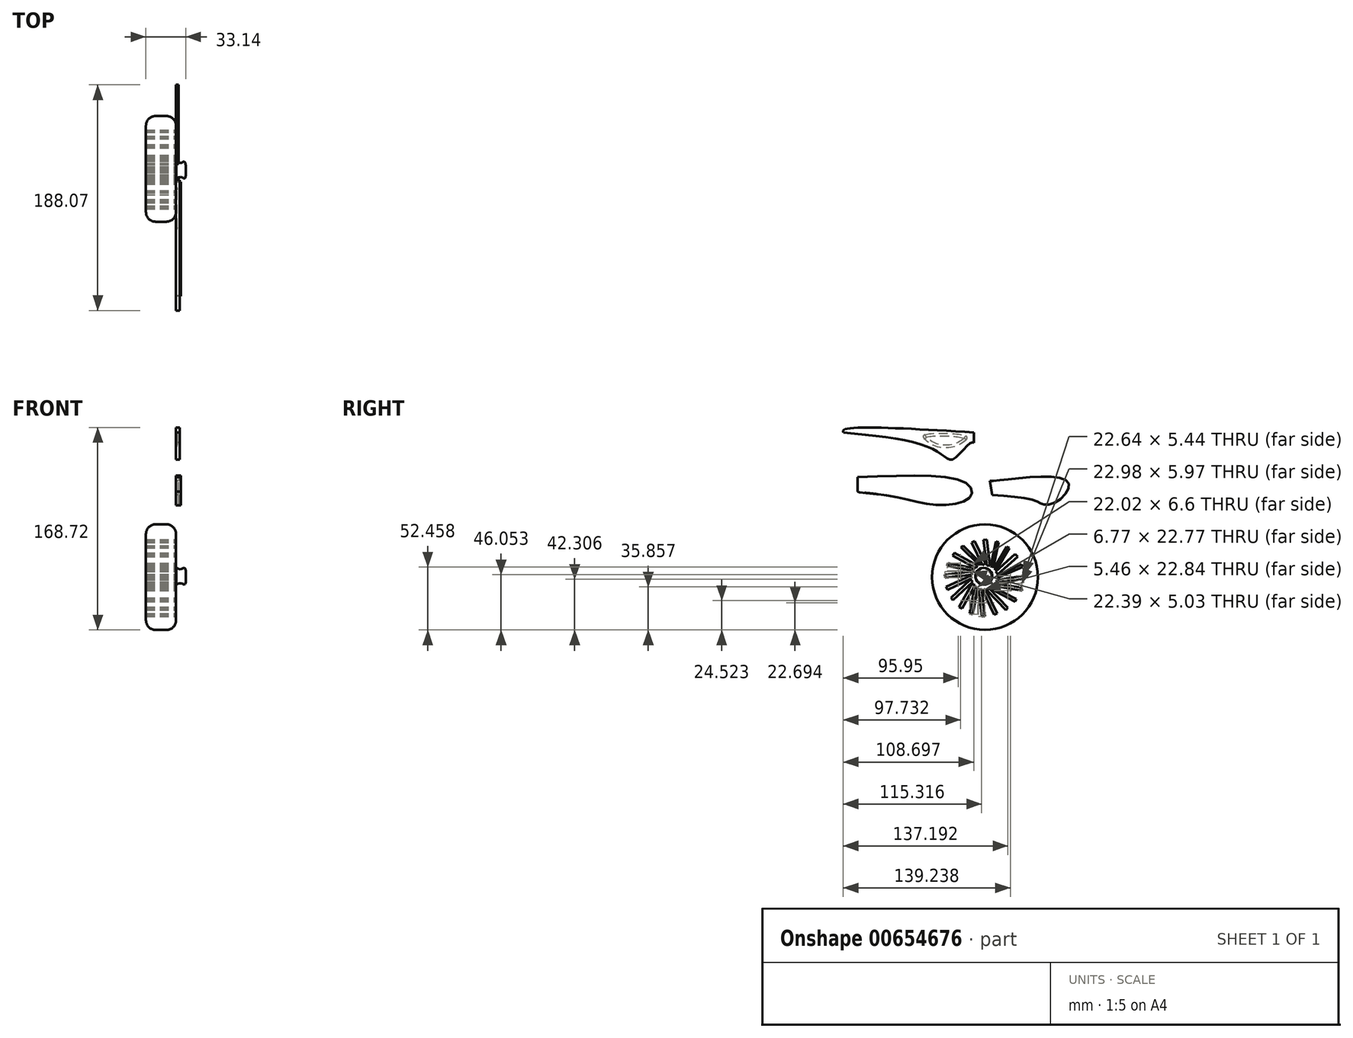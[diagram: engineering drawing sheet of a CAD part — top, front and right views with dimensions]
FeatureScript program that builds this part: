
annotation { "Feature Type Name" : "Feature", "Feature Type Description" : "" }
export const myFeature = defineFeature(function(context is Context, id is Id, definition is map)
    precondition{}
    {
        {
            var Q0;
            Q0=qCreatedBy(makeId("Right.planeOp"),FACE);
            var sketch = newSketch(context, id + "F0", { "sketchPlane" : qUnion([Q0])});
            skFitSpline(sketch, "E0", {"points": [v(-61.2, 25.53) * mm, v(9.14, 13.55) * mm, v(24.54, 4.13) * mm, v(30.7, 3.62) * mm, v(44.56, 16.97) * mm, v(47.3, 16.8) * mm], "startDerivative": vector(208.43, -21.43) * mm, "endDerivative": vector(29.28, -15.69) * mm});
            skFitSpline(sketch, "E1", {"points": [v(-61.2, 25.53) * mm, v(-61.2, 27.58) * mm, v(47.3, 25.53) * mm], "startDerivative": vector(-7.46, 18.15) * mm, "endDerivative": vector(177.67, -10.83) * mm});
            skLineSegment(sketch, "E2", {"start": v(47.3, 16.8) * mm, "end": v(47.3, 25.53) * mm});
            skSolve(sketch);
        }
        {
            var Q0;
            Q0=makeQuery(id+"F0.imprint","IMPRINT",FACE,{"disambiguationData":[TD([[makeQuery(id+"F0.imprint","IMPRINT",EDGE,{"derivedFrom":sQuery(id+"F0.wireOp",EDGE,"E0")}),1.0]])]});
            extrude(context, id + "F1", {"entities" : qUnion([Q0]), "depth" : 3 * mm, "offsetDistance" : 25.4 * mm});
        }
        {
            var Q0;
            Q0=qCreatedBy(makeId("Right.planeOp"),FACE);
            var sketch = newSketch(context, id + "F2", { "sketchPlane" : qUnion([Q0])});
            skFitSpline(sketch, "E3", {"points": [v(5.41, 21.07) * mm, v(5.19, 21.5) * mm, v(5.02, 22.27) * mm, v(5.24, 22.9) * mm, v(6.38, 23.6) * mm, v(8.34, 24.16) * mm, v(11.68, 24.6) * mm, v(16.33, 24.87) * mm, v(18.57, 24.92) * mm, v(23.05, 24.91) * mm, v(27.45, 24.72) * mm, v(32.7, 24.28) * mm, v(36.42, 23.76) * mm, v(38.73, 23.22) * mm, v(40.53, 22.6) * mm, v(41.13, 22.23) * mm, v(41.55, 21.71) * mm, v(41.66, 21.04) * mm, v(41.41, 20.27) * mm, v(40.6, 19.08) * mm, v(38.85, 17.67) * mm, v(36.95, 16.38) * mm, v(34.7, 15.13) * mm, v(32.34, 14.11) * mm, v(29.64, 13.3) * mm, v(26.9, 12.82) * mm, v(23.76, 12.62) * mm, v(20.63, 12.82) * mm, v(17.77, 13.37) * mm, v(14.7, 14.36) * mm, v(12.81, 15.2) * mm, v(10.72, 16.4) * mm, v(9.05, 17.5) * mm, v(7.02, 19.16) * mm, v(6.25, 19.87) * mm, v(5.41, 21.07) * mm]});
            skSolve(sketch);
        }
        {
            var Q0;
            Q0=qCreatedBy(makeId("Right.planeOp"),FACE);
            var sketch = newSketch(context, id + "F3", { "sketchPlane" : qUnion([Q0])});
            skCircle(sketch, "E4", {"center": v(56.51, -95.04) * mm, "radius": 44.03 * mm});
            skSolve(sketch);
        }
        {
            var Q0;
            Q0 = qSketchRegion(id + "F3", true);
            extrude(context, id + "F4", {"entities" : qUnion([Q0]), "oppositeDirection" : true, "depth" : 25 * mm, "offsetDistance" : 25 * mm});
        }
        {
            var Q0;
            Q0=makeQuery(id+"F4.opExtrude","SWEPT_FACE",FACE,{"disambiguationData":[OSD([sQuery(id+"F3.wireOp",EDGE,"E4")])]});
            fillet(context, id + "F5", {"entities" : qUnion([Q0]), "radius" : 8 * mm, "tangentPropagation" : true, "allowEdgeOverflow" : false});
        }
        {
            var Q0;
            Q0=qCreatedBy(makeId("Right.planeOp"),FACE);
            var sketch = newSketch(context, id + "F6", { "sketchPlane" : qUnion([Q0])});
            skLineSegment(sketch, "E5", {"start": v(36.45, -70.1) * mm, "end": v(38.25, -68.9) * mm});
            skLineSegment(sketch, "E6", {"start": v(38.25, -68.9) * mm, "end": v(53.15, -83.57) * mm});
            skLineSegment(sketch, "E7", {"start": v(53.15, -83.57) * mm, "end": v(51.66, -85.08) * mm});
            skLineSegment(sketch, "E8", {"start": v(51.66, -85.08) * mm, "end": v(36.45, -70.1) * mm});
            skLineSegment(sketch, "E9", {"start": v(30.92, -74.91) * mm, "end": v(50.15, -85.25) * mm});
            skLineSegment(sketch, "E10", {"start": v(50.15, -85.25) * mm, "end": v(48.95, -87.49) * mm});
            skLineSegment(sketch, "E11", {"start": v(48.95, -87.49) * mm, "end": v(29.5, -77.03) * mm});
            skLineSegment(sketch, "E12", {"start": v(29.5, -77.03) * mm, "end": v(30.92, -74.91) * mm});
            skLineSegment(sketch, "E13", {"start": v(25.67, -83.3) * mm, "end": v(47.2, -87.49) * mm});
            skLineSegment(sketch, "E14", {"start": v(47.2, -87.49) * mm, "end": v(46.72, -89.9) * mm});
            skLineSegment(sketch, "E15", {"start": v(46.72, -89.9) * mm, "end": v(25.17, -85.71) * mm});
            skLineSegment(sketch, "E16", {"start": v(25.17, -85.71) * mm, "end": v(25.67, -83.3) * mm});
            skLineSegment(sketch, "E17", {"start": v(23.2, -92.92) * mm, "end": v(45.34, -90.5) * mm});
            skLineSegment(sketch, "E18", {"start": v(45.34, -90.5) * mm, "end": v(45.6, -92.8) * mm});
            skLineSegment(sketch, "E19", {"start": v(45.6, -92.8) * mm, "end": v(23.56, -95.52) * mm});
            skLineSegment(sketch, "E20", {"start": v(23.56, -95.52) * mm, "end": v(23.2, -92.92) * mm});
            skLineSegment(sketch, "E21", {"start": v(24.02, -103.15) * mm, "end": v(44.38, -93.78) * mm});
            skLineSegment(sketch, "E22", {"start": v(44.38, -93.78) * mm, "end": v(45.45, -96.1) * mm});
            skLineSegment(sketch, "E23", {"start": v(45.45, -96.1) * mm, "end": v(25.25, -105.63) * mm});
            skLineSegment(sketch, "E24", {"start": v(25.25, -105.63) * mm, "end": v(24.02, -103.15) * mm});
            skLineSegment(sketch, "E25", {"start": v(29.97, -114.23) * mm, "end": v(46.3, -99.12) * mm});
            skLineSegment(sketch, "E26", {"start": v(46.3, -99.12) * mm, "end": v(44.55, -97.23) * mm});
            skLineSegment(sketch, "E27", {"start": v(44.55, -97.23) * mm, "end": v(28.13, -112.42) * mm});
            skLineSegment(sketch, "E28", {"start": v(28.13, -112.42) * mm, "end": v(29.97, -114.23) * mm});
            skLineSegment(sketch, "E29", {"start": v(37.28, -121.33) * mm, "end": v(48.11, -102) * mm});
            skLineSegment(sketch, "E30", {"start": v(48.11, -102) * mm, "end": v(45.77, -100.73) * mm});
            skLineSegment(sketch, "E31", {"start": v(45.77, -100.73) * mm, "end": v(34.94, -120.05) * mm});
            skLineSegment(sketch, "E32", {"start": v(34.94, -120.05) * mm, "end": v(37.28, -121.31) * mm});
            skLineSegment(sketch, "E33", {"start": v(43.76, -125.47) * mm, "end": v(48, -103.15) * mm});
            skLineSegment(sketch, "E34", {"start": v(48, -103.15) * mm, "end": v(50.53, -103.63) * mm});
            skLineSegment(sketch, "E35", {"start": v(50.53, -103.63) * mm, "end": v(46.3, -125.92) * mm});
            skLineSegment(sketch, "E36", {"start": v(46.3, -125.92) * mm, "end": v(43.76, -125.47) * mm});
            skLineSegment(sketch, "E37", {"start": v(56.5, -127.45) * mm, "end": v(53.72, -104.95) * mm});
            skLineSegment(sketch, "E38", {"start": v(53.72, -104.95) * mm, "end": v(51.04, -105.28) * mm});
            skLineSegment(sketch, "E39", {"start": v(51.04, -105.28) * mm, "end": v(53.82, -127.79) * mm});
            skLineSegment(sketch, "E40", {"start": v(53.82, -127.79) * mm, "end": v(56.5, -127.45) * mm});
            skLineSegment(sketch, "E41", {"start": v(54.64, -106.19) * mm, "end": v(56.94, -105.08) * mm});
            skLineSegment(sketch, "E42", {"start": v(56.94, -105.08) * mm, "end": v(66.62, -125.2) * mm});
            skLineSegment(sketch, "E43", {"start": v(66.62, -125.2) * mm, "end": v(64.08, -126.42) * mm});
            skLineSegment(sketch, "E44", {"start": v(64.08, -126.42) * mm, "end": v(54.64, -106.19) * mm});
            skLineSegment(sketch, "E45", {"start": v(58.3, -106.19) * mm, "end": v(59.91, -104.4) * mm});
            skLineSegment(sketch, "E46", {"start": v(59.91, -104.4) * mm, "end": v(75.63, -120.64) * mm});
            skLineSegment(sketch, "E47", {"start": v(75.63, -120.64) * mm, "end": v(73.82, -122.39) * mm});
            skLineSegment(sketch, "E48", {"start": v(73.82, -122.39) * mm, "end": v(58.3, -106.19) * mm});
            skLineSegment(sketch, "E49", {"start": v(61.1, -104.66) * mm, "end": v(62.82, -103) * mm});
            skLineSegment(sketch, "E50", {"start": v(62.82, -103) * mm, "end": v(82.6, -113.24) * mm});
            skLineSegment(sketch, "E51", {"start": v(82.6, -113.24) * mm, "end": v(81.45, -115.47) * mm});
            skLineSegment(sketch, "E52", {"start": v(81.45, -115.47) * mm, "end": v(61.1, -104.66) * mm});
            skLineSegment(sketch, "E53", {"start": v(64.41, -102.36) * mm, "end": v(64.15, -100.22) * mm});
            skLineSegment(sketch, "E54", {"start": v(64.15, -100.22) * mm, "end": v(86.85, -103.9) * mm});
            skLineSegment(sketch, "E55", {"start": v(86.85, -103.9) * mm, "end": v(87.13, -106.19) * mm});
            skLineSegment(sketch, "E56", {"start": v(87.13, -106.19) * mm, "end": v(64.41, -102.36) * mm});
            skLineSegment(sketch, "E57", {"start": v(66.37, -99.47) * mm, "end": v(66.37, -97.26) * mm});
            skLineSegment(sketch, "E58", {"start": v(66.37, -97.26) * mm, "end": v(88.63, -94.03) * mm});
            skLineSegment(sketch, "E59", {"start": v(88.63, -94.03) * mm, "end": v(89, -96.6) * mm});
            skLineSegment(sketch, "E60", {"start": v(89, -96.6) * mm, "end": v(66.37, -99.47) * mm});
            skLineSegment(sketch, "E61", {"start": v(67.3, -95.65) * mm, "end": v(66.37, -94.12) * mm});
            skPoint(sketch, "E61.startSnap0", {"position": v(77.5, -95.65) * mm});
            skLineSegment(sketch, "E62", {"start": v(66.37, -94.12) * mm, "end": v(86.85, -84.43) * mm});
            skLineSegment(sketch, "E63", {"start": v(86.85, -84.43) * mm, "end": v(87.93, -86.7) * mm});
            skLineSegment(sketch, "E64", {"start": v(87.93, -86.7) * mm, "end": v(67.3, -95.65) * mm});
            skLineSegment(sketch, "E65", {"start": v(65.43, -90.5) * mm, "end": v(67.3, -92.6) * mm});
            skLineSegment(sketch, "E66", {"start": v(67.3, -92.6) * mm, "end": v(83.66, -78.01) * mm});
            skLineSegment(sketch, "E67", {"start": v(83.66, -78.01) * mm, "end": v(81.7, -75.83) * mm});
            skLineSegment(sketch, "E68", {"start": v(81.7, -75.83) * mm, "end": v(65.43, -90.5) * mm});
            skLineSegment(sketch, "E69", {"start": v(74.61, -69.64) * mm, "end": v(76.82, -70.66) * mm});
            skLineSegment(sketch, "E70", {"start": v(76.82, -70.66) * mm, "end": v(65.94, -88.94) * mm});
            skLineSegment(sketch, "E71", {"start": v(65.94, -88.94) * mm, "end": v(63.98, -87.76) * mm});
            skLineSegment(sketch, "E72", {"start": v(63.98, -87.76) * mm, "end": v(74.61, -69.64) * mm});
            skLineSegment(sketch, "E73", {"start": v(67.9, -65.9) * mm, "end": v(63.56, -86.56) * mm});
            skLineSegment(sketch, "E74", {"start": v(63.56, -86.56) * mm, "end": v(61.26, -86.07) * mm});
            skLineSegment(sketch, "E75", {"start": v(61.26, -86.07) * mm, "end": v(65.6, -65.45) * mm});
            skLineSegment(sketch, "E76", {"start": v(65.6, -65.45) * mm, "end": v(67.9, -65.9) * mm});
            skLineSegment(sketch, "E77", {"start": v(58.04, -85.2) * mm, "end": v(60.6, -85.2) * mm});
            skLineSegment(sketch, "E78", {"start": v(60.6, -85.2) * mm, "end": v(58.04, -63.87) * mm});
            skLineSegment(sketch, "E79", {"start": v(58.04, -63.87) * mm, "end": v(55.26, -64.2) * mm});
            skLineSegment(sketch, "E80", {"start": v(55.26, -64.2) * mm, "end": v(58.04, -85.2) * mm});
            skLineSegment(sketch, "E81", {"start": v(56.85, -83.58) * mm, "end": v(48.01, -64.97) * mm});
            skLineSegment(sketch, "E82", {"start": v(48.01, -64.97) * mm, "end": v(45.5, -66.16) * mm});
            skLineSegment(sketch, "E83", {"start": v(45.5, -66.16) * mm, "end": v(54.53, -85.2) * mm});
            skLineSegment(sketch, "E84", {"start": v(54.53, -85.2) * mm, "end": v(56.85, -83.58) * mm});
            skSolve(sketch);
        }
        {
            var Q0;
            Q0 = qSketchRegion(id + "F6", true);
            extrude(context, id + "F7", {"entities" : qUnion([Q0]), "operationType" : NewBodyOperationType.REMOVE, "oppositeDirection" : true, "depth" : 25 * mm, "offsetDistance" : 25 * mm});
        }
        {
            var Q0;
            Q0=makeQuery(id+"F2.imprint","IMPRINT",FACE,{"disambiguationData":[TD([[makeQuery(id+"F2.imprint","IMPRINT",EDGE,{"derivedFrom":sQuery(id+"F2.wireOp",EDGE,"E3")}),-1.0]])]});
            var Q1;
            Q1=sQuery(id+"F2.wireOp",EDGE,"E3");
            extrude(context, id + "F8", {"entities" : qUnion([Q0]), "operationType" : NewBodyOperationType.REMOVE, "surfaceEntities" : qUnion([Q1]), "depth" : 1 * mm, "offsetDistance" : 25 * mm});
        }
        {
            var Q0;
            Q0=makeQuery(id+"F8.boolean.opBoolean","COPY",EDGE,{"derivedFrom":makeQuery(id+"F8.opExtrude","CAP_EDGE",EDGE,{"disambiguationData":[OSD([sQuery(id+"F2.wireOp",EDGE,"E3")])],"isStart":false})});
            fillet(context, id + "F9", {"entities" : qUnion([Q0]), "radius" : 3 * mm, "tangentPropagation" : true, "allowEdgeOverflow" : false});
        }
        {
            var Q0;
            Q0=qCreatedBy(makeId("Right.planeOp"),FACE);
            var sketch = newSketch(context, id + "F10", { "sketchPlane" : qUnion([Q0])});
            skFitSpline(sketch, "E85", {"points": [v(-49.4, -11.79) * mm, v(41.96, -17.45) * mm, v(44.39, -28.16) * mm, v(17.7, -35.03) * mm, v(-21.5, -27.55) * mm, v(-49.4, -23.92) * mm, v(-49.6, -23.71) * mm], "startDerivative": vector(377.5, 15.7) * mm, "endDerivative": vector(-4.15, 11.37) * mm});
            skLineSegment(sketch, "E86", {"start": v(-49.6, -23.71) * mm, "end": v(-49.4, -11.79) * mm});
            skSolve(sketch);
        }
        {
            var Q0;
            Q0=qCreatedBy(makeId("Right.planeOp"),FACE);
            var sketch = newSketch(context, id + "F11", { "sketchPlane" : qUnion([Q0])});
            skFitSpline(sketch, "E87", {"points": [v(62.61, -26.45) * mm, v(98.8, -31.3) * mm, v(104.66, -34.33) * mm, v(115.57, -32.52) * mm, v(126.49, -19.38) * mm, v(120.22, -12.7) * mm, v(77.57, -13.31) * mm, v(60.6, -14.93) * mm, v(60.19, -14.73) * mm], "startDerivative": vector(225.47, -17.56) * mm, "endDerivative": vector(-11.9, 10.58) * mm});
            skLineSegment(sketch, "E88", {"start": v(62.61, -26.45) * mm, "end": v(60.6, -14.93) * mm});
            skSolve(sketch);
        }
        {
            var Q0;
            Q0 = qSketchRegion(id + "F10", true);
            extrude(context, id + "F12", {"entities" : qUnion([Q0]), "depth" : 4 * mm, "offsetDistance" : 25 * mm});
        }
        {
            var Q0;
            Q0 = qSketchRegion(id + "F11", true);
            extrude(context, id + "F13", {"entities" : qUnion([Q0]), "depth" : 2 * mm, "offsetDistance" : 25 * mm});
        }
        {
            var Q0;
            Q0=qCreatedBy(makeId("Top.planeOp"),FACE);
            var sketch = newSketch(context, id + "F14", { "sketchPlane" : qUnion([Q0])});
            skLineSegment(sketch, "E89", {"start": v(34.7, 31.2) * mm, "end": v(34.7, 38.2) * mm});
            skFitSpline(sketch, "E90", {"points": [v(34.7, 38.2) * mm, v(36.42, 37.38) * mm, v(37.82, 37.14) * mm, v(39.76, 37.38) * mm, v(40.78, 38.2) * mm, v(41.65, 38.2) * mm, v(42.47, 36.85) * mm, v(42.66, 34.19) * mm, v(42.66, 31.92) * mm, v(42.66, 31.29) * mm], "startDerivative": vector(14.48, -7.78) * mm, "endDerivative": vector(0, -7.51) * mm});
            skLineSegment(sketch, "E91", {"start": v(34.7, 31.2) * mm, "end": v(42.66, 31.29) * mm});
            skSolve(sketch);
        }
        {
            var Q0;
            Q0=makeQuery(id+"F14.imprint","IMPRINT",FACE,{"disambiguationData":[TD([[makeQuery(id+"F14.imprint","IMPRINT",EDGE,{"derivedFrom":sQuery(id+"F14.wireOp",EDGE,"E89")}),-1.0]])]});
            var Q1;
            Q1=sQuery(id+"F14.wireOp",EDGE,"E91");
            revolve(context, id + "F15", {"entities" : qUnion([Q0]), "axis" : qUnion([Q1]), "revolveType" : RevolveType.FULL});
        }
        {
            var Q0;
            Q0=makeQuery(id+"F15.opRevolve","SWEPT_BODY",BODY,{"disambiguationData":[OSD([sQuery(id+"F14.wireOp",EDGE,"E89"),sQuery(id+"F14.wireOp",EDGE,"E90"),sQuery(id+"F14.wireOp",EDGE,"E91")])]});
            transform(context, id + "F16", {"entities" : qUnion([Q0]), "transformType" : TransformType.TRANSLATION_3D, "dx" : -34.6 * mm, "dy" : 24.3 * mm, "dz" : -94.3 * mm, "makeCopy" : false});
        }
    });
